# Revit family: ledpanelrc-g_re166-21w-dali-4000-wh-ct_140046188
name_source: partatom
category: Leuchten
revit_build: Autodesk Revit 2016 (Build: 20190508_0715(x64)
units: mm (PartAtom-declared; Revit-internal decimal feet)

## family parameters
Basisbauteil = Fläche
Beim Laden mit Abzugskörper schneiden = Nein
Bemaßung runder Anschluss = Durchmesser verwenden
Gemeinsam genutzt = Nein
Lichtquelle = Nein
Raumberechnungspunkt = Nein
Teiletyp = Normal

## types (1)
- LEDPanelRc-G Re166-21W-DALI-4000-WH-CT (1 x LED, 1900 lm)
    Approval mark = CE, ENEC
    Beschreibung = Design low glare LED panel. Comfortable lighting for study and work environment (UGR < 16). Significantly lower energy consumption up to 65%.
    CIE Flux Codes = 71 96 99 100 100
    Control Gear = Electronic ballast
    Height = 0 mm  [stored 0 ft]
    Hersteller = OPPLE
    Lamp Light Flux = 1900 lm
    Lamp count = 1
    Lampe = 1 x LED
    Length = 1198 mm
    Luminous efficacy = 86 lm/W
    ModVariant = Nein
    Modell = 140046188
    Mounting Place = Ceiling
    Mounting Type = Surface mounted, Recessed
    Number of Poles = 1
    OnlyDefault = Ja
    Power Factor = 1
    Product Name = LEDPanelRc-G Re166-21W-DALI-4000-WH-CT
    Product group = Panel Grille
    ProductGroupID = 410
    Protection Class = Protection class I
    Protection Degree = IP 20
    RLX_Detail_Level = 1
    RlxData = <blob elided: 17465 chars, md5=a9e56874>
    Scheinlast = 22 VA
    Socket = socket
    Standby Power = 0 W
    System Light Flux = 1900 lm
    System Power = 22 W
    Typenbild = 140046188.jpg
    Typenkommentare = Product without accessories
    URL = http://relux.com
    VarID = ---
    Voltage = 0 V
    Vorgabe-Ansicht = 1800 mm
    Weight = 0.00 kg
    Width = 166 mm

note: [stored X ft] marks values corroborated as IEEE doubles in the binary element streams (Revit-internal decimal feet)

## geometry (parser evidence)
native form markers: Blend x4, Sweep x12
no freeform markers — native parametric forms only
